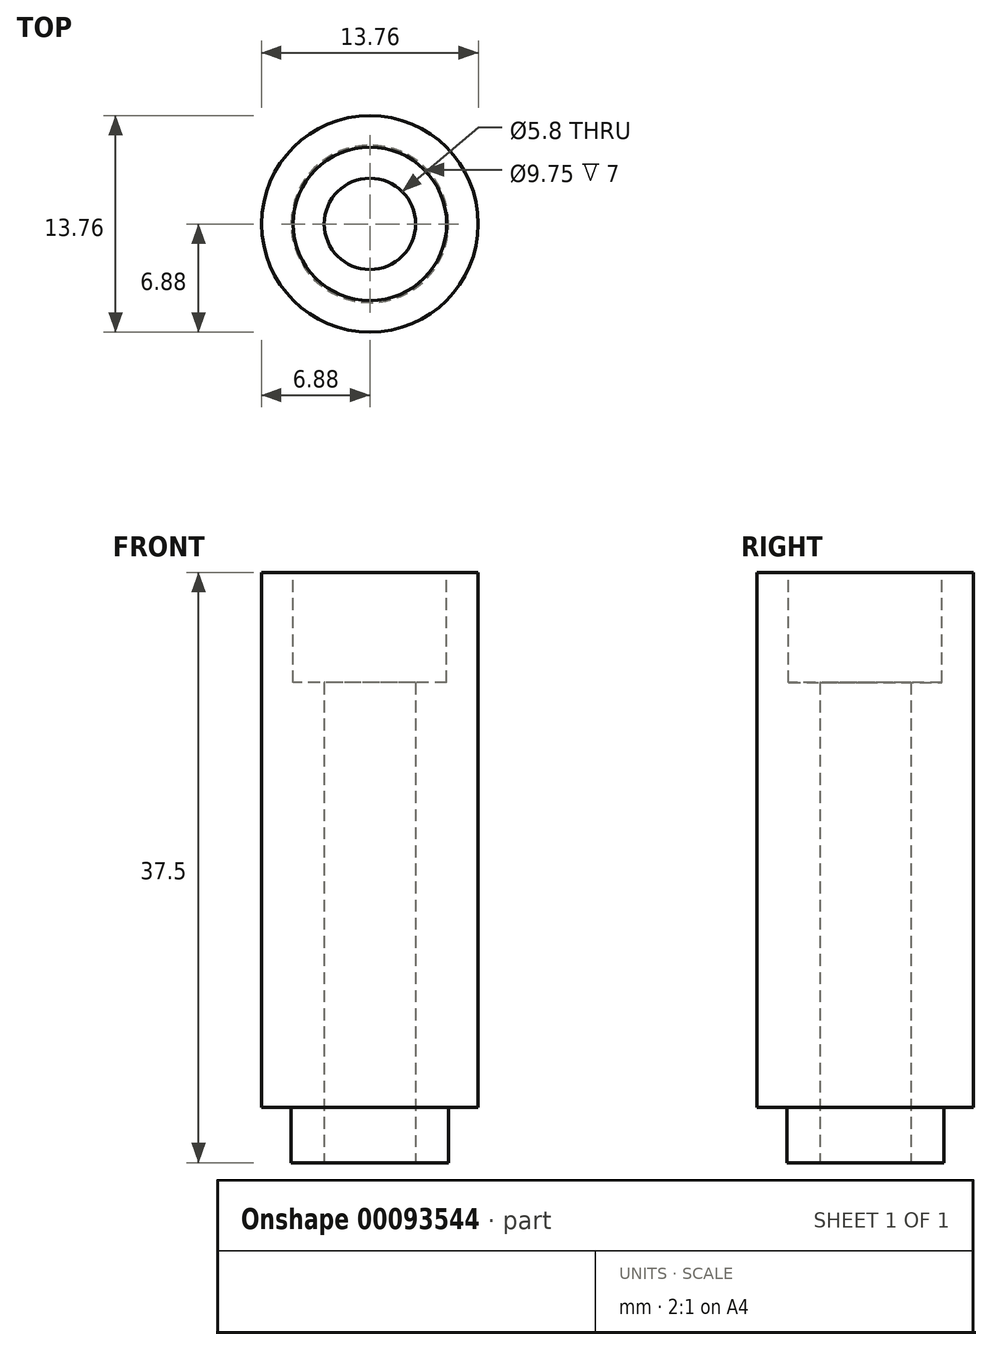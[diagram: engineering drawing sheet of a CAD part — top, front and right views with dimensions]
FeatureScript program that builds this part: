
annotation { "Feature Type Name" : "Feature", "Feature Type Description" : "" }
export const myFeature = defineFeature(function(context is Context, id is Id, definition is map)
    precondition{}
    {
        {
            var Q0;
            Q0=qCreatedBy(makeId("Top.planeOp"),FACE);
            var sketch = newSketch(context, id + "F0", { "sketchPlane" : qUnion([Q0])});
            skCircle(sketch, "E0", {"center": v(0, 0) * mm, "radius": 6.88 * mm});
            skCircle(sketch, "E1", {"center": v(0, 0) * mm, "radius": 2.9 * mm});
            skSolve(sketch);
        }
        {
            var Q0;
            Q0 = qSketchRegion(id + "F0", true);
            extrude(context, id + "F1", {"entities" : qUnion([Q0]), "depth" : 34 * mm, "offsetDistance" : 25 * mm});
        }
        {
            var Q0;
            Q0=makeQuery(id+"F1.opExtrude","CAP_FACE",FACE,{"disambiguationData":[OSD([sQuery(id+"F0.wireOp",EDGE,"E0"),sQuery(id+"F0.wireOp",EDGE,"E1")])],"isStart":true});
            var sketch = newSketch(context, id + "F2", { "sketchPlane" : qUnion([Q0])});
            skCircle(sketch, "E2", {"center": v(0, 0) * mm, "radius": 5 * mm});
            skCircle(sketch, "E3.0", {"center": v(0, 0) * mm, "radius": 2.9 * mm});
            skSolve(sketch);
        }
        {
            var Q0;
            Q0 = qSketchRegion(id + "F2", true);
            extrude(context, id + "F3", {"entities" : qUnion([Q0]), "operationType" : NewBodyOperationType.ADD, "depth" : 3.5 * mm, "offsetDistance" : 25 * mm});
        }
        {
            var Q0;
            Q0=makeQuery(id+"F1.opExtrude","CAP_FACE",FACE,{"disambiguationData":[OSD([sQuery(id+"F0.wireOp",EDGE,"E0"),sQuery(id+"F0.wireOp",EDGE,"E1")])],"isStart":false});
            var sketch = newSketch(context, id + "F4", { "sketchPlane" : qUnion([Q0])});
            skCircle(sketch, "E4", {"center": v(0, 0) * mm, "radius": 4.88 * mm});
            skSolve(sketch);
        }
        {
            var Q0;
            Q0 = qSketchRegion(id + "F4", true);
            extrude(context, id + "F5", {"entities" : qUnion([Q0]), "operationType" : NewBodyOperationType.REMOVE, "oppositeDirection" : true, "depth" : 7 * mm, "offsetDistance" : 25 * mm});
        }
    });
